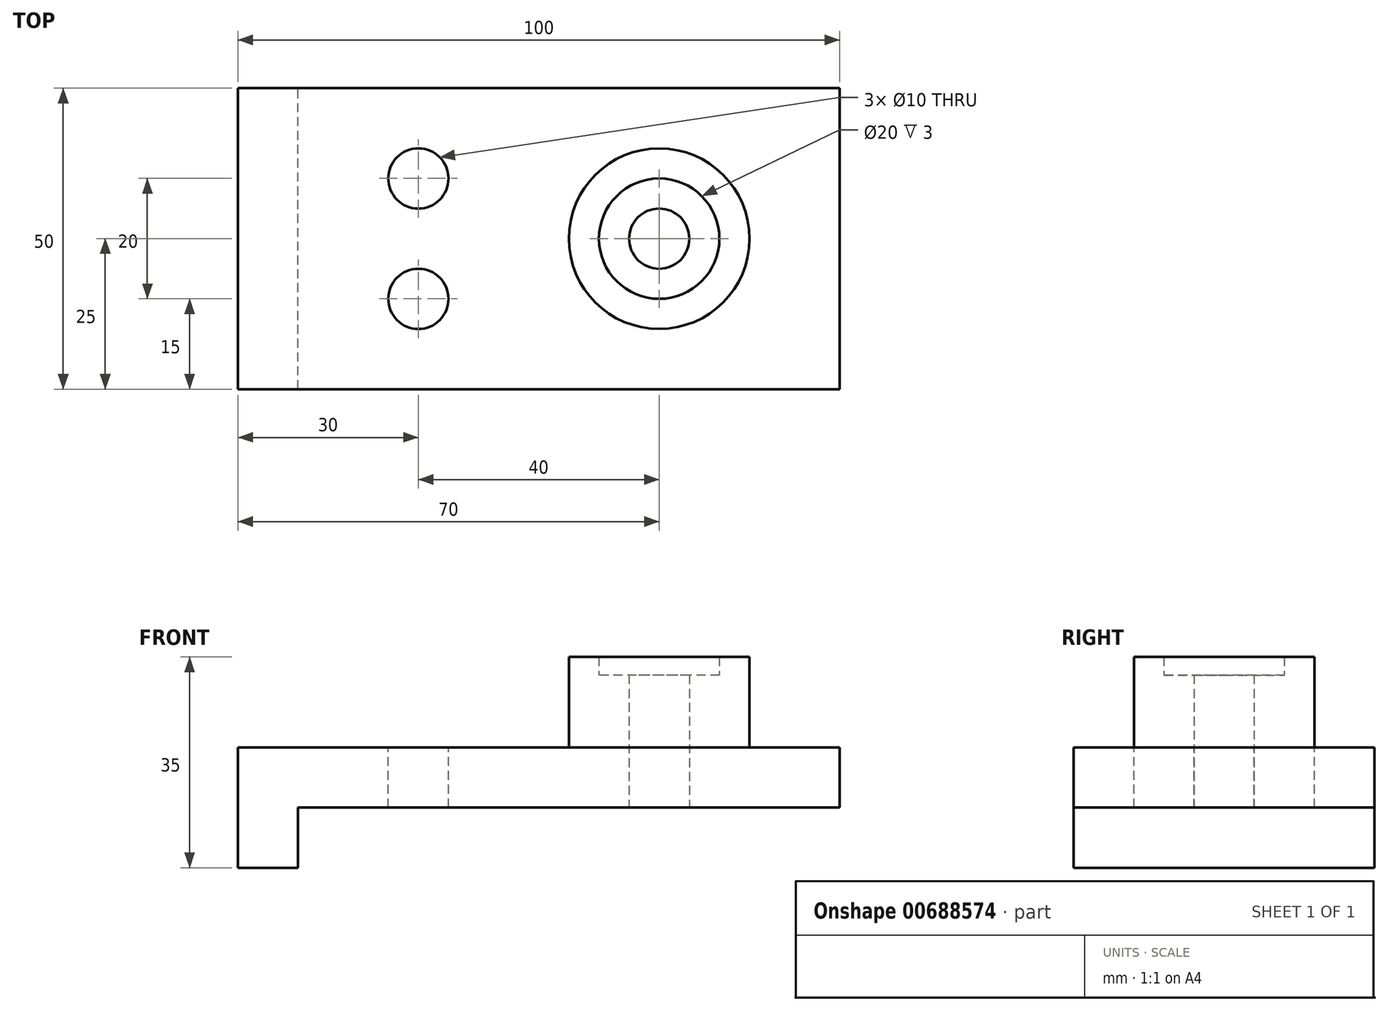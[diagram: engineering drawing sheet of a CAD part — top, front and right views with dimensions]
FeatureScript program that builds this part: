
annotation { "Feature Type Name" : "Feature", "Feature Type Description" : "" }
export const myFeature = defineFeature(function(context is Context, id is Id, definition is map)
    precondition{}
    {
        {
            var Q0;
            Q0=qCreatedBy(makeId("Front.planeOp"),FACE);
            var sketch = newSketch(context, id + "F0", { "sketchPlane" : qUnion([Q0])});
            skLineSegment(sketch, "E0", {"start": v(0, 0) * mm, "end": v(10, 0) * mm});
            skLineSegment(sketch, "E1", {"start": v(10, 0) * mm, "end": v(10, 10) * mm});
            skLineSegment(sketch, "E2", {"start": v(10, 10) * mm, "end": v(100, 10) * mm});
            skLineSegment(sketch, "E3", {"start": v(100, 10) * mm, "end": v(100, 20) * mm});
            skLineSegment(sketch, "E4", {"start": v(100, 20) * mm, "end": v(0, 20) * mm});
            skLineSegment(sketch, "E5", {"start": v(0, 20) * mm, "end": v(0, 0) * mm});
            skSolve(sketch);
        }
        {
            var Q0;
            Q0 = qSketchRegion(id + "F0", true);
            extrude(context, id + "F1", {"entities" : qUnion([Q0]), "depth" : 50 * mm, "offsetDistance" : 25 * mm});
        }
        {
            var Q0;
            Q0=makeQuery(id+"F1.opExtrude","SWEPT_FACE",FACE,{"disambiguationData":[OSD([sQuery(id+"F0.wireOp",EDGE,"E4")])]});
            var sketch = newSketch(context, id + "F2", { "sketchPlane" : qUnion([Q0])});
            skCircle(sketch, "E6", {"center": v(70, -25) * mm, "radius": 15 * mm});
            skPoint(sketch, "E6.centerSnap0", {"position": v(100, -25) * mm});
            skCircle(sketch, "E7", {"center": v(70, -25) * mm, "radius": 10 * mm});
            skCircle(sketch, "E8", {"center": v(70, -25) * mm, "radius": 5 * mm});
            skCircle(sketch, "E9", {"center": v(30, -15) * mm, "radius": 5 * mm});
            skCircle(sketch, "E10", {"center": v(30, -35) * mm, "radius": 5 * mm});
            skSolve(sketch);
        }
        {
            var Q0;
            Q0=makeQuery(id+"F2.imprint","IMPRINT",FACE,{"disambiguationData":[TD([[makeQuery(id+"F2.imprint","IMPRINT",EDGE,{"derivedFrom":sQuery(id+"F2.wireOp",EDGE,"E6")}),1.0]])]});
            extrude(context, id + "F3", {"entities" : qUnion([Q0]), "operationType" : NewBodyOperationType.ADD, "depth" : 15 * mm, "offsetDistance" : 25 * mm});
        }
        {
            var Q0;
            Q0=makeQuery(id+"F2.imprint","IMPRINT",FACE,{"disambiguationData":[TD([[makeQuery(id+"F2.imprint","IMPRINT",EDGE,{"derivedFrom":sQuery(id+"F2.wireOp",EDGE,"E7")}),1.0]])]});
            extrude(context, id + "F4", {"entities" : qUnion([Q0]), "operationType" : NewBodyOperationType.ADD, "depth" : 12 * mm, "offsetDistance" : 25 * mm});
        }
        {
            var Q0;
            Q0=makeQuery(id+"F2.imprint","IMPRINT",FACE,{"disambiguationData":[TD([[makeQuery(id+"F2.imprint","IMPRINT",EDGE,{"derivedFrom":sQuery(id+"F2.wireOp",EDGE,"E8")}),1.0]])]});
            var Q1;
            Q1=makeQuery(id+"F2.imprint","IMPRINT",FACE,{"disambiguationData":[TD([[makeQuery(id+"F2.imprint","IMPRINT",EDGE,{"derivedFrom":sQuery(id+"F2.wireOp",EDGE,"E10")}),1.0]])]});
            var Q2;
            Q2=makeQuery(id+"F2.imprint","IMPRINT",FACE,{"disambiguationData":[TD([[makeQuery(id+"F2.imprint","IMPRINT",EDGE,{"derivedFrom":sQuery(id+"F2.wireOp",EDGE,"E9")}),1.0]])]});
            extrude(context, id + "F5", {"entities" : qUnion([Q0, Q1, Q2]), "operationType" : NewBodyOperationType.REMOVE, "oppositeDirection" : true, "depth" : 25 * mm, "offsetDistance" : 25 * mm});
        }
    });
